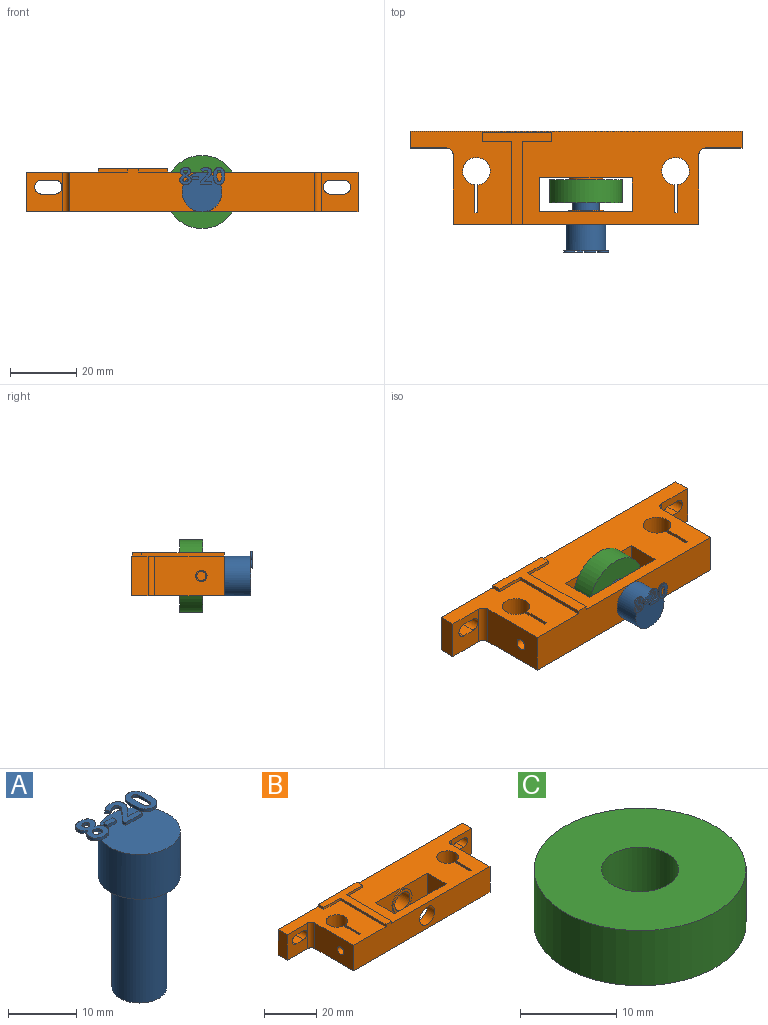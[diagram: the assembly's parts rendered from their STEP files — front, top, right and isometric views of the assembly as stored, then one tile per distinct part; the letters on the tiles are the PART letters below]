
ASSEMBLY  parts=3 mates=2
PART A: 89 faces, bbox 13.6x13.4x28.5 mm
  f0: plane 0.75x0.57mm, normal (0,0,1), area 0.1mm2, adj f5,f78,f79
  f1: plane 12x12mm, normal (0,0,1), area 100.3mm2, adj f5,f22,f23,f24,f25,f26,f40,f41
  f2: plane 1.04x0.97mm, normal (0,0,1), area 0.5mm2, adj f5,f29,f30,f31,f32,f33
  f3: cylinder r=4mm len=20mm, axis (0,0,-1), area 502.7mm2, adj f4,f6
  f4: plane 8x8mm, normal (0,0,-1), area 50.3mm2, adj f3
  f5: cylinder r=6mm len=12mm, axis (0,0,-1), area 301.6mm2, adj f0,f1,f2,f6,f39,f70,f88
  f6: plane 12x12mm, normal (0,0,-1), area 62.8mm2, adj f3,f5
  f7: extruded ~0.5x0.43mm, area 0.2mm2, adj f8,f37,f38,f39
  f8: extruded ~0.5x0.43mm, area 0.2mm2, adj f7,f9,f38,f39
  f9: extruded ~0.5x0.37mm, area 0.2mm2, adj f8,f10,f38,f39
  f10: extruded ~0.5x0.38mm, area 0.2mm2, adj f9,f11,f38,f39
  f11: extruded ~0.5x0.46mm, area 0.3mm2, adj f10,f12,f38,f39
  f12: extruded ~0.5x0.47mm, area 0.3mm2, adj f11,f13,f38,f39
  f13: extruded ~0.5x0.36mm, area 0.2mm2, adj f12,f37,f38,f39
  f14: extruded ~1.15x0.5mm, area 0.6mm2, adj f15,f35,f38,f39
  f15: extruded ~1.15x0.5mm, area 0.6mm2, adj f14,f16,f38,f39
  f16: extruded ~0.86x0.5mm, area 0.5mm2, adj f15,f17,f38,f39
  f17: extruded ~0.67x0.5mm, area 0.4mm2, adj f16,f18,f38,f39
  f18: extruded ~0.61x0.57mm, area 0.4mm2, adj f17,f19,f38,f39
  f19: extruded ~0.72x0.58mm, area 0.5mm2, adj f18,f20,f38,f39
  f20: extruded ~0.75x0.5mm, area 0.4mm2, adj f19,f21,f38,f39
  f21: extruded ~0.98x0.5mm, area 0.6mm2, adj f20,f22,f38,f39
  f22: extruded ~1.28x0.5mm, area 0.7mm2, adj f1,f21,f23,f38,f39
  f23: extruded ~1.26x0.5mm, area 0.7mm2, adj f1,f22,f24,f38
  f24: extruded ~0.98x0.5mm, area 0.6mm2, adj f1,f23,f25,f38
  f25: extruded ~0.71x0.5mm, area 0.4mm2, adj f1,f24,f26,f38
  f26: extruded ~0.8x0.62mm, area 0.5mm2, adj f1,f25,f27,f38,f39
  f27: extruded ~0.68x0.53mm, area 0.4mm2, adj f26,f28,f38,f39
  f28: extruded ~0.68x0.5mm, area 0.4mm2, adj f27,f35,f38,f39
  f29: extruded ~0.62x0.5mm, area 0.4mm2, adj f2,f30,f36,f38,f39
  f30: extruded ~0.5x0.43mm, area 0.2mm2, adj f2,f29,f31,f38
  f31: extruded ~0.5x0.44mm, area 0.2mm2, adj f2,f30,f32,f38
  f32: extruded ~0.58x0.5mm, area 0.3mm2, adj f2,f31,f33,f38
  f33: extruded ~0.56x0.5mm, area 0.3mm2, adj f2,f32,f34,f38,f39
  f34: extruded ~0.5x0.45mm, area 0.3mm2, adj f33,f36,f38,f39
  f35: extruded ~0.87x0.5mm, area 0.5mm2, adj f14,f28,f38,f39
  f36: extruded ~0.84x0.72mm, area 0.6mm2, adj f29,f34,f38,f39
  f37: extruded ~0.5x0.37mm, area 0.2mm2, adj f7,f13,f38,f39
  f38: plane 5.09x3.48mm, normal (0,0,1), area 11.2mm2, adj f7,f8,f9,f10,f11,f12,f13,f14
  f39: plane 5.05x3.32mm, normal (0,0,-1), area 8.6mm2, adj f5,f7,f8,f9,f10,f11,f12,f13
  f40: plane 0.85x0.5mm, normal (-1,0,0), area 0.4mm2, adj f1,f41,f43,f44
  f41: plane 1.82x0.5mm, normal (0,-1,0), area 0.9mm2, adj f1,f40,f42,f44
  f42: plane 0.85x0.5mm, normal (1,0,0), area 0.4mm2, adj f1,f41,f43,f44
  f43: plane 1.82x0.5mm, normal (0,1,0), area 0.9mm2, adj f1,f40,f42,f44
  f44: plane 1.82x0.85mm, normal (0,0,1), area 1.5mm2, adj f40,f41,f42,f43
  f45: extruded ~0.5x0.39mm, area 0.2mm2, adj f1,f46,f68,f69,f70
  f46: extruded ~0.5x0.41mm, area 0.2mm2, adj f1,f45,f47,f69
  f47: extruded ~0.78x0.72mm, area 0.5mm2, adj f1,f46,f48,f69
  f48: plane 1.26x1.24mm, normal (-0.71,0.7,0), area 0.9mm2, adj f1,f47,f49,f69
  f49: plane 0.73x0.5mm, normal (-1,0,0), area 0.4mm2, adj f1,f48,f50,f69
  f50: plane 3.46x0.5mm, normal (0,-1,0), area 1.7mm2, adj f1,f49,f51,f69
  f51: plane 0.88x0.5mm, normal (1,0,0), area 0.4mm2, adj f1,f50,f52,f69
  f52: plane 2.16x0.5mm, normal (0,1,0), area 1.1mm2, adj f1,f51,f53,f69
  f53: plane 0.5x0.05mm, normal (1,0,0), area 0mm2, adj f1,f52,f54,f69
  f54: plane 0.64x0.6mm, normal (0.69,-0.73,0), area 0.4mm2, adj f1,f53,f55,f69
  f55: extruded ~0.9x0.89mm, area 0.6mm2, adj f1,f54,f56,f69
  f56: extruded ~0.62x0.5mm, area 0.4mm2, adj f1,f55,f57,f69,f70
  f57: extruded ~0.64x0.5mm, area 0.3mm2, adj f56,f58,f69,f70
  f58: extruded ~0.7x0.5mm, area 0.4mm2, adj f57,f59,f69,f70
  f59: extruded ~0.55x0.5mm, area 0.4mm2, adj f58,f60,f69,f70
  f60: extruded ~0.82x0.5mm, area 0.4mm2, adj f59,f61,f69,f70
  f61: extruded ~0.64x0.5mm, area 0.3mm2, adj f60,f62,f69,f70
  f62: extruded ~0.53x0.5mm, area 0.3mm2, adj f61,f63,f69,f70
  f63: extruded ~0.61x0.5mm, area 0.4mm2, adj f62,f64,f69,f70
  f64: plane 0.67x0.57mm, normal (-0.76,-0.65,0), area 0.4mm2, adj f63,f65,f69,f70
  f65: extruded ~0.57x0.5mm, area 0.3mm2, adj f64,f66,f69,f70
  f66: extruded ~0.56x0.5mm, area 0.3mm2, adj f65,f67,f69,f70
  f67: extruded ~0.5x0.44mm, area 0.2mm2, adj f66,f68,f69,f70
  f68: extruded ~0.5x0.44mm, area 0.2mm2, adj f45,f67,f69,f70
  f69: plane 5.03x3.48mm, normal (0,0,1), area 9.1mm2, adj f45,f46,f47,f48,f49,f50,f51,f52
  f70: plane 3.34x2.04mm, normal (0,0,-1), area 3.5mm2, adj f5,f45,f56,f57,f58,f59,f60,f61
  f71: extruded ~1.92x0.5mm, area 1mm2, adj f72,f86,f87,f88
  f72: extruded ~1.91x0.5mm, area 1mm2, adj f71,f73,f87,f88
  f73: extruded ~1.3x0.65mm, area 0.8mm2, adj f72,f74,f87,f88
  f74: extruded ~1.3x0.62mm, area 0.8mm2, adj f73,f75,f87,f88
  f75: extruded ~1.93x0.5mm, area 1mm2, adj f1,f74,f76,f87,f88
  f76: extruded ~1.9x0.5mm, area 1mm2, adj f1,f75,f77,f87
  f77: extruded ~1.29x0.64mm, area 0.8mm2, adj f1,f76,f86,f87
  f78: extruded ~0.53x0.5mm, area 0.4mm2, adj f0,f79,f85,f87,f88
  f79: extruded ~1.31x0.5mm, area 0.7mm2, adj f0,f78,f80,f87,f88
  f80: extruded ~1.31x0.5mm, area 0.7mm2, adj f79,f81,f87,f88
  f81: extruded ~0.53x0.5mm, area 0.4mm2, adj f80,f82,f87,f88
  f82: extruded ~0.53x0.5mm, area 0.4mm2, adj f81,f83,f87,f88
  f83: extruded ~1.31x0.5mm, area 0.7mm2, adj f82,f84,f87,f88
  f84: extruded ~1.3x0.5mm, area 0.7mm2, adj f83,f85,f87,f88
  f85: extruded ~0.53x0.5mm, area 0.4mm2, adj f78,f84,f87,f88
  f86: extruded ~1.31x0.62mm, area 0.8mm2, adj f1,f71,f77,f87,f88
  f87: plane 5.1x3.46mm, normal (0,0,1), area 10.7mm2, adj f71,f72,f73,f74,f75,f76,f77,f78
  f88: plane 5.1x3.46mm, normal (0,0,-1), area 8.4mm2, adj f5,f71,f72,f73,f74,f75,f78,f79
PART B: 53 faces, bbox 100x28x13 mm
  f0: plane 4.68x0.88mm, normal (0,1,0), area 4.1mm2, adj f2,f12,f14,f46
  f1: plane 100x28mm, normal (0,0,1), area 1655.1mm2, adj f3,f4,f5,f6,f7,f8,f9,f10
  f2: plane 100x28mm, normal (0,0,-1), area 1795.1mm2, adj f0,f3,f4,f5,f6,f7,f8,f9
  f3: plane 100x12mm, normal (0,1,0), area 1138.7mm2, adj f1,f2,f5,f10,f19,f20,f21,f22
  f4: plane 12x11mm, normal (0,-1,0), area 101.3mm2, adj f1,f2,f10,f23,f24,f25,f26,f48
  f5: plane 12x5mm, normal (-1,0,0), area 60mm2, adj f1,f2,f3,f6
  f6: plane 12x11mm, normal (0,-1,0), area 101.3mm2, adj f1,f2,f5,f19,f20,f21,f22,f52
  f7: plane 21x12mm, normal (-1,0,0), area 242.9mm2, adj f1,f2,f8,f51,f52
  f8: plane 74x13mm, normal (0,-1,0), area 838.4mm2, adj f1,f2,f7,f9,f27,f38,f39,f45
  f9: plane 21x12mm, normal (1,0,0), area 245.8mm2, adj f1,f2,f8,f46,f48
  f10: plane 12x5mm, normal (1,0,0), area 60mm2, adj f1,f2,f3,f4
  f11: cylinder r=4.15mm len=12mm, axis (0,0,1), area 302.4mm2, adj f1,f2,f12,f14
  f12: plane 12x8.45mm, normal (1,0,0), area 99.6mm2, adj f0,f1,f2,f11,f13,f46
  f13: plane 4.68x0.88mm, normal (0,1,0), area 4.1mm2, adj f1,f12,f14,f46
  f14: plane 12x8.45mm, normal (-1,0,0), area 99.6mm2, adj f0,f1,f2,f11,f13,f46
  f15: plane 12x8.45mm, normal (-1,0,0), area 95.3mm2, adj f1,f2,f16,f18,f49
  f16: cylinder r=4.15mm len=12mm, axis (0,0,1), area 302.4mm2, adj f1,f2,f15,f17
  f17: plane 12x8.45mm, normal (1,0,0), area 92.3mm2, adj f1,f2,f16,f18,f51
  f18: plane 12x0.88mm, normal (0,1,0), area 10.5mm2, adj f1,f2,f15,f17
  f19: cylinder r=2.1mm len=5mm, axis (0,1,0), area 33mm2, adj f3,f6,f20,f22
  f20: plane 5x4mm, normal (0,0,1), area 20mm2, adj f3,f6,f19,f21
  f21: cylinder r=2.1mm len=5mm, axis (0,1,0), area 33mm2, adj f3,f6,f20,f22
  f22: plane 5x4mm, normal (0,0,-1), area 20mm2, adj f3,f6,f19,f21
  f23: plane 5x4mm, normal (0,0,-1), area 20mm2, adj f3,f4,f24,f26
  f24: cylinder r=2.1mm len=5mm, axis (0,1,0), area 33mm2, adj f3,f4,f23,f25
  f25: plane 5x4mm, normal (0,0,1), area 20mm2, adj f3,f4,f24,f26
  f26: cylinder r=2.1mm len=5mm, axis (0,1,0), area 33mm2, adj f3,f4,f23,f25
  f27: cylinder r=4.1mm len=8.2mm, axis (0,-1,0), area 110.8mm2, adj f8,f37
  f28: plane 12x10.2mm, normal (1,0,0), area 122.4mm2, adj f1,f2,f30,f31
  f29: plane 12x10.2mm, normal (-1,0,0), area 122.4mm2, adj f1,f2,f30,f31
  f30: plane 28x12mm, normal (0,-1,0), area 251.2mm2, adj f1,f2,f28,f29,f32
  f31: plane 28x12mm, normal (0,1,0), area 249.3mm2, adj f1,f2,f28,f29,f36
  f32: cylinder r=5.2mm len=10.39mm, axis (0,1,0), area 16.3mm2, adj f30,f33
  f33: plane 10.39x10.39mm, normal (0,-1,0), area 32mm2, adj f32,f35
  f34: plane 8.2x8.2mm, normal (0,-1,0), area 52.8mm2, adj f35
  f35: cylinder r=4.1mm len=8.2mm, axis (0,-1,0), area 167.4mm2, adj f33,f34
  f36: cylinder r=5.25mm len=10.51mm, axis (0,-1,0), area 16.5mm2, adj f31,f37
  f37: plane 10.51x10.51mm, normal (0,1,0), area 33.9mm2, adj f27,f36
  f38: plane 24.9x1mm, normal (-1,0,0), area 24.9mm2, adj f1,f8,f44,f45
  f39: plane 24.9x1mm, normal (1,0,0), area 24.9mm2, adj f1,f8,f40,f45
  f40: plane 8.79x1mm, normal (0,-1,0), area 8.8mm2, adj f1,f39,f41,f45
  f41: plane 2.87x1mm, normal (1,0,0), area 2.9mm2, adj f1,f40,f42,f45
  f42: plane 20.81x1mm, normal (0,1,0), area 20.8mm2, adj f1,f41,f43,f45
  f43: plane 2.87x1mm, normal (-1,0,0), area 2.9mm2, adj f1,f42,f44,f45
  f44: plane 8.79x1mm, normal (0,-1,0), area 8.8mm2, adj f1,f38,f43,f45
  f45: plane 27.76x20.81mm, normal (0,0,1), area 140mm2, adj f8,f38,f39,f40,f41,f42,f43,f44
  f46: cylinder r=1.4mm len=18mm, axis (1,0,0), area 155.3mm2, adj f0,f9,f12,f13,f14,f47
  f47: plane 2.8x2.8mm, normal (1,0,0), area 6.2mm2, adj f46
  f48: cylinder r=2mm len=12mm, axis (0,0,1), area 37.7mm2, adj f1,f2,f4,f9
  f49: cylinder r=1.4mm len=10.56mm, axis (-1,0,0), area 92.9mm2, adj f15,f50
  f50: plane 2.8x2.8mm, normal (-1,0,0), area 6.2mm2, adj f49
  f51: cylinder r=1.7mm len=6.56mm, axis (-1,0,0), area 70.1mm2, adj f7,f17
  f52: cylinder r=2mm len=12mm, axis (0,0,1), area 37.7mm2, adj f1,f2,f6,f7
PART C: 4 faces, bbox 22x22x7 mm
  f0: cylinder r=4mm len=8mm, axis (0,0,-1), area 175.9mm2, adj f2,f3
  f1: cylinder r=11mm len=22mm, axis (0,0,-1), area 483.8mm2, adj f2,f3
  f2: plane 22x22mm, normal (0,0,1), area 329.9mm2, adj f0,f1
  f3: plane 22x22mm, normal (0,0,-1), area 329.9mm2, adj f0,f1
PLACE A rot(axis=(1,0,0),90deg) t=(5.95,9.74,6.05)mm
PLACE B t=(-0.7,5.43,0.05)mm
PLACE C rot(axis=(-1,0,0),90deg) t=(5.95,-3.76,6.05)mm
MATE fastened C.f0 <-> B.f27  axis (0,1,0) through (5.95,3.24,6.05)mm
MATE fastened A.f3 <-> B.f27  axis (0,1,0) through (5.95,-10.26,6.05)mm
